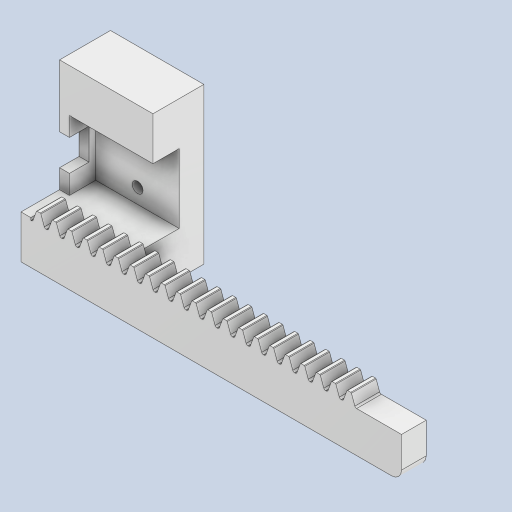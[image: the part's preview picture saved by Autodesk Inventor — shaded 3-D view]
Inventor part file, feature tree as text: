
AUTODESK INVENTOR PART (.ipt)
format: ipt  version: 2023 (Build 270158000, 158)  size: 436,736 bytes
history: native  units: mm
features: extrude x6, sketch x6, pattern_linear x1, chamfer x1, hole x1, fillet x1
ambient origin geometry x8: Origin, YZ Plane, XZ Plane, XY Plane, X Axis, Y Axis, Z Axis, Center Point
bodies: Solid1 (feature_tree)
feature tree (16):
  extrude  "Extrusion1"  Depth=10.0mm TaperAngle=0.0deg
  extrude  "Extrusion2"  Depth=10.0mm TaperAngle=0.0deg
  pattern_linear  "Rectangular Pattern1"  Spacing1=0.1mm  [1 undecoded]
  chamfer  "面取り1"  Distance=10.5mm
  extrude  "押し出し7"  Depth=75.0mm
  extrude  "押し出し10"  Depth=14.0mm
  hole  "穴1"  [1 undecoded]
  extrude  "押し出し11"  Depth=16.9mm TaperAngle=0.0deg
  extrude  "押し出し12"  Depth=2.0mm TaperAngle=0.0deg
  fillet  "フィレット1"  Radius=8.0mm
  sketch  "Sketch_1"  dims[d0=5.0mm d1=0.0mm d2=10.0mm d3=0.0mm d4=220.0mm d6=3.142mm d7=10.0mm d9=0.0mm d10=0.1mm d11=2.0mm d12=45.0deg d13=10.5mm d14=75.0mm d37=14.0mm d43=5.0mm d58=16.9mm d59=0.0mm d80=2.0mm d81=0.0mm d88=8.0mm d90=8.5mm d91=8.5mm d92=2.2mm d93=6.0mm d94=4.2mm d95=1.0mm d96=90.0deg d97=8.0mm d98=20.594885mm d102=4.5mm d103=4.0mm d105=10.0mm d107=10.0mm d108=20.0mm d110=23.5mm d113=6.0mm d114=0.0mm d115=5.0mm d116=0.0mm d117=2.0mm d118=31.5mm d121=8.75mm d124=1.35mm d125=6.3mm d126=15.75mm d129=8.9mm d131=2.8mm d134=10.3mm d135=11.75mm]
  sketch  "スケッチ5"
  sketch  "スケッチ9"
  sketch  "スケッチ10"
  sketch  "スケッチ11"
  sketch  "スケッチ12"
note: 2 required parameter values undecoded (feature->parameter linkage not recoverable at this tier; creation-order binding heuristic only, values carry confidence <= 0.55)
